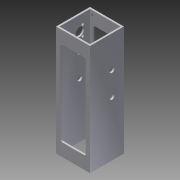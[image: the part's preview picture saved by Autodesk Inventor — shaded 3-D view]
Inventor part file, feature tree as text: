
AUTODESK INVENTOR PART (.ipt)
format: ipt  version: 2015 (Build 190159000, 159)  size: 194,048 bytes
history: native  units: mm
features: sketch x7, hole x5, thread x4, extrude x2, other x1, fillet x1, pattern_circular x1
ambient origin geometry x8: Origin, YZ Plane, XZ Plane, XY Plane, X Axis, Y Axis, Z Axis, Center Point
bodies: Body1 (feature_tree)
feature tree (21):
  other  "ソリッド1"
  extrude  "押し出し1"  Depth=40.0mm
  extrude  "押し出し2"  Depth=40.0mm
  fillet  "フィレット1"  Radius=2.0mm
  hole  "穴1"  [1 undecoded]
  thread  "ねじ1"
  thread  "ねじ2"
  thread  "ねじ3"
  thread  "ねじ4"
  hole  "穴2"  [1 undecoded]
  hole  "穴3"  [1 undecoded]
  hole  "穴4"  [1 undecoded]
  pattern_circular  "円形状パターン1"  [2 undecoded]
  hole  "穴5"  [1 undecoded]
  sketch  "スケッチ1"
  sketch  "スケッチ3"
  sketch  "スケッチ4"
  sketch  "スケッチ5"
  sketch  "スケッチ6"
  sketch  "スケッチ7"
  sketch  "スケッチ8"
note: 7 required parameter values undecoded (feature->parameter linkage not recoverable at this tier; creation-order binding heuristic only, values carry confidence <= 0.55)
